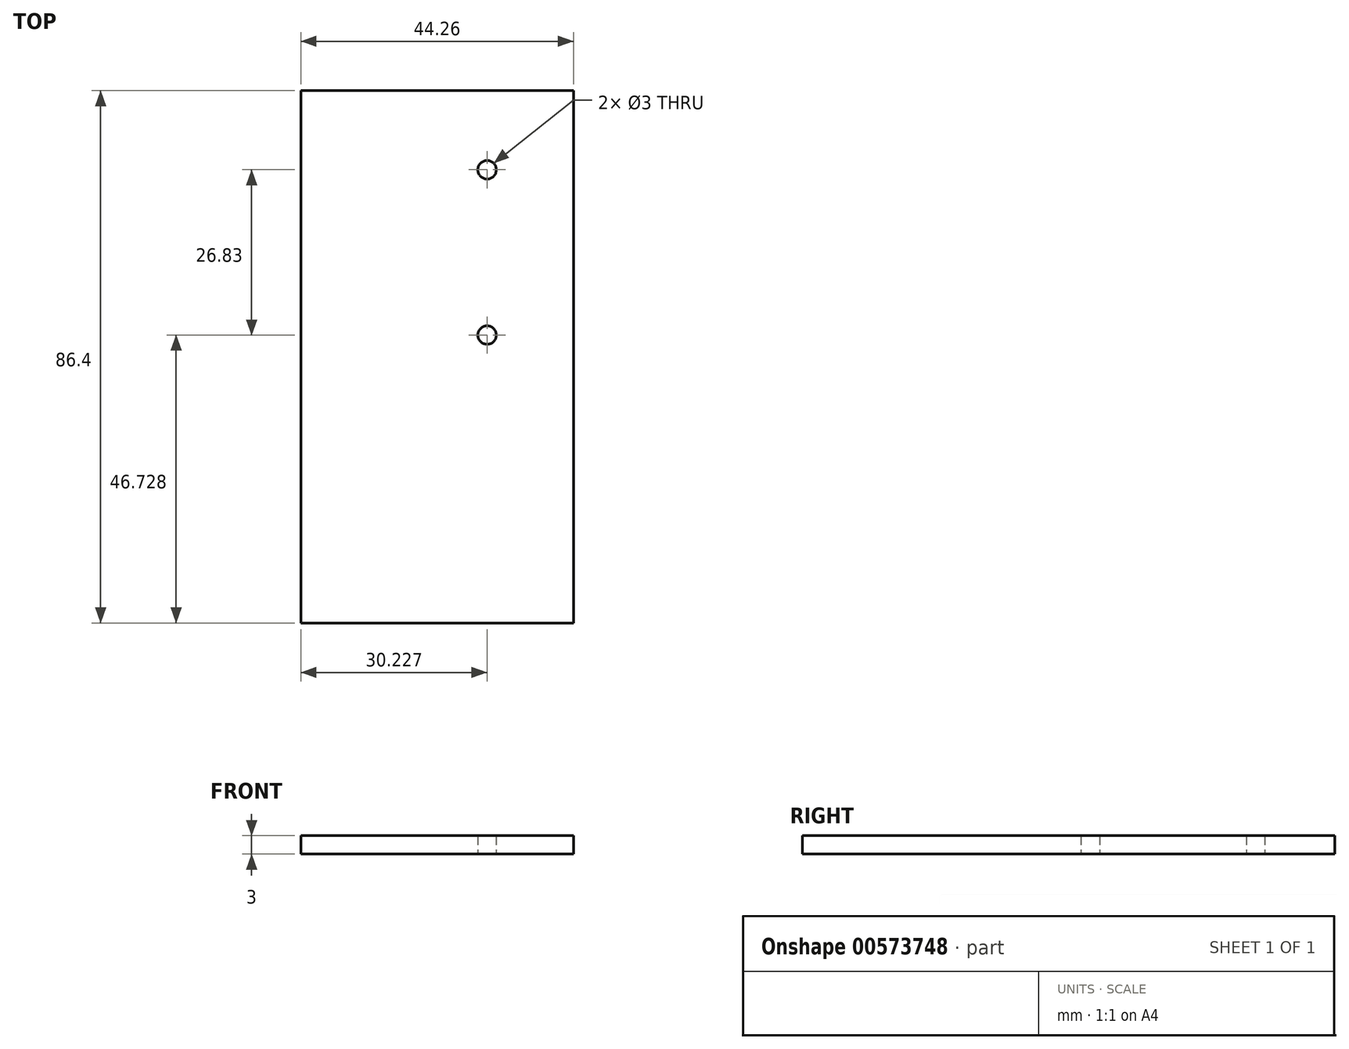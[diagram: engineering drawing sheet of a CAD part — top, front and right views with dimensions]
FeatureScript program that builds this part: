
annotation { "Feature Type Name" : "Feature", "Feature Type Description" : "" }
export const myFeature = defineFeature(function(context is Context, id is Id, definition is map)
    precondition{}
    {
        {
            var Q0;
            Q0=qCreatedBy(makeId("Top.planeOp"),FACE);
            var sketch = newSketch(context, id + "F0", { "sketchPlane" : qUnion([Q0])});
            skLineSegment(sketch, "E0.bottom", {"start": v(0, 0) * mm, "end": v(44.26, 0) * mm});
            skLineSegment(sketch, "E0.top", {"start": v(0, 86.4) * mm, "end": v(44.26, 86.4) * mm});
            skLineSegment(sketch, "E0.left", {"start": v(0, 0) * mm, "end": v(0, 86.4) * mm});
            skLineSegment(sketch, "E0.right", {"start": v(44.26, 0) * mm, "end": v(44.26, 86.4) * mm});
            skSolve(sketch);
        }
        {
            var Q0;
            Q0=makeQuery(id+"F0.imprint","IMPRINT",FACE,{"disambiguationData":[TD([[makeQuery(id+"F0.imprint","IMPRINT",EDGE,{"derivedFrom":sQuery(id+"F0.wireOp",EDGE,"E0.bottom")}),1.0]])]});
            extrude(context, id + "F1", {"entities" : qUnion([Q0]), "depth" : 3 * mm, "offsetDistance" : 25.4 * mm});
        }
        {
            var Q0;
            Q0 = qSketchRegion(id + "F0", true);
            var sketch = newSketch(context, id + "F2", { "sketchPlane" : qUnion([Q0])});
            skLineSegment(sketch, "E1", {"start": v(30.23, 73.56) * mm, "end": v(30.23, 46.73) * mm});
            skSolve(sketch);
        }
        {
            var Q0;
            Q0=sQuery(id+"F2.wireOp",VERTEX,"E1.start");
            var Q1;
            Q1=sQuery(id+"F2.wireOp",VERTEX,"E1.end");
            var Q2;
            Q2=makeQuery(id+"F1.opExtrude","SWEPT_BODY",BODY,{"disambiguationData":[OSD([sQuery(id+"F0.wireOp",EDGE,"E0.bottom"),sQuery(id+"F0.wireOp",EDGE,"E0.top"),sQuery(id+"F0.wireOp",EDGE,"E0.left"),sQuery(id+"F0.wireOp",EDGE,"E0.right")])]});
            hole(context, id + "F3", {"style" : HoleStyle.SIMPLE, "endStyle" : HoleEndStyle.THROUGH, "oppositeDirection" : true, "holeDiameter" : 3 * mm, "isTappedThrough" : true, "tappedDepth" : 12.7 * mm, "tapClearance" : 3, "locations" : qUnion([Q0, Q1]), "scope" : qUnion([Q2])});
        }
    });
